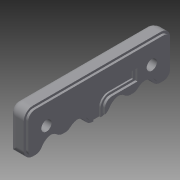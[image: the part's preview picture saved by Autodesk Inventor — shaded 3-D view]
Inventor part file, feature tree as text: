
AUTODESK INVENTOR PART (.ipt)
format: ipt  version: 2015 (Build 190159000, 159)  size: 260,096 bytes
history: native  units: in
note: dims shown in document units (in); Inventor stores cm internally (conversion verified against a paired STEP export)
features: extrude x4, sketch x4, projected_geometry x3, fillet x1, other x1
ambient origin geometry x8: Origin, YZ Plane, XZ Plane, XY Plane, X Axis, Y Axis, Z Axis, Center Point
bodies: Solid1 (feature_tree)
feature tree (13):
  extrude  "Extrusion1"  Depth=2.0in
  extrude  "Extrusion2"  Depth=0.1in
  fillet  "Fillet1"  Radius=0.125in
  other  "Lip1"
  extrude  "Extrusion3"  Depth=0.125in
  extrude  "Extrusion4"  Depth=0.138in
  sketch  "Sketch1"  dims[d0=0.6in d1=2.0in]
  sketch  "Sketch2"  dims[d2=0.25in d3=0.0in d4=0.1in d5=0.125in]
  projected_geometry  "Projected Loop1"
  sketch  "Sketch3"  dims[d6=0.05in d7=0.0in d8=0.125in]
  projected_geometry  "Projected Loop2"
  sketch  "Sketch4"  dims[d9=0.03in d10=0.03in d11=0.0in d12=0.0in d13=0.0in d14=0.0in d15=0.1406in d16=0.1406in d17=0.25in d18=0.25in d19=1.0in d20=0.0in d21=0.223in d22=0.138in d23=0.0in]
  projected_geometry  "Projected Loop3"
